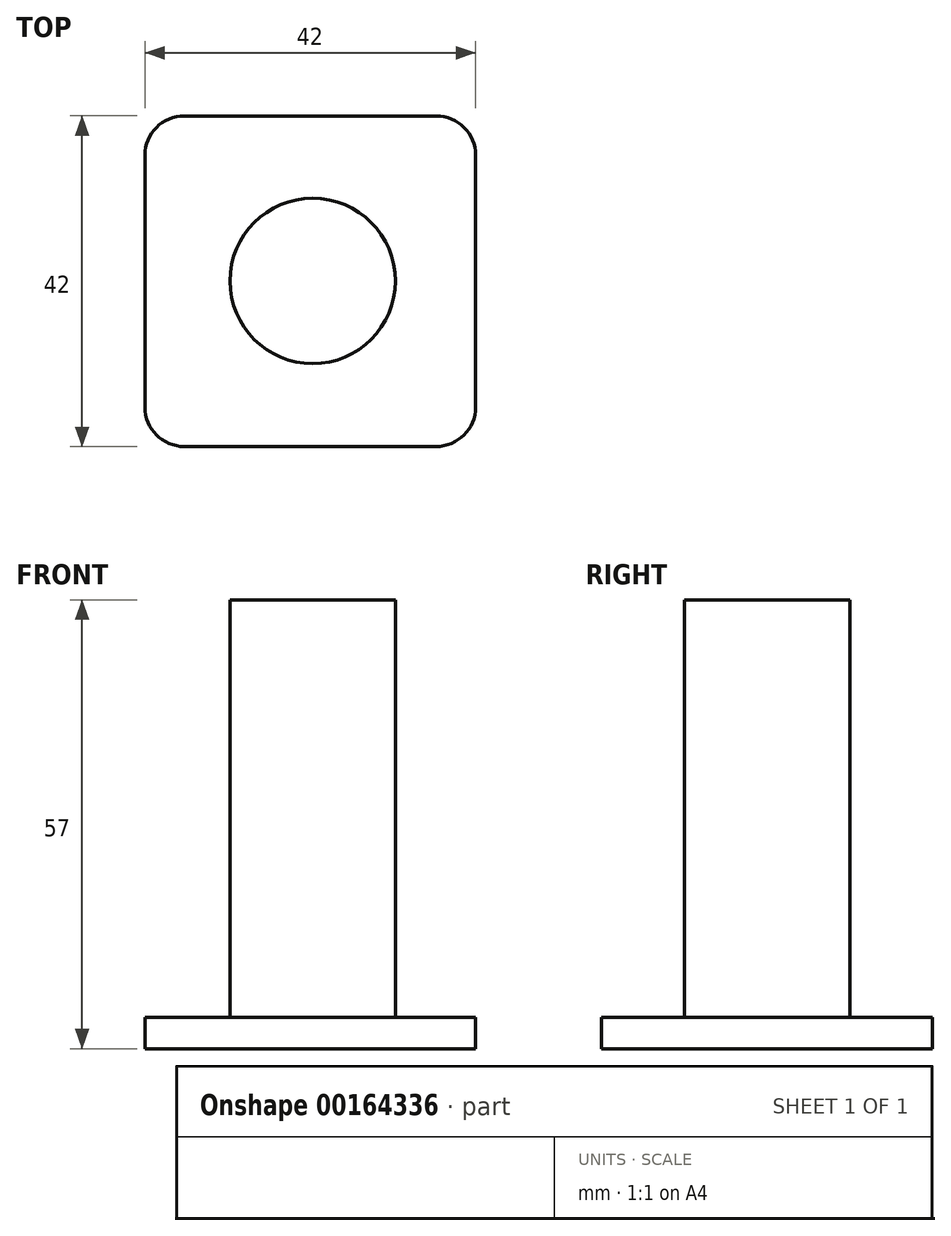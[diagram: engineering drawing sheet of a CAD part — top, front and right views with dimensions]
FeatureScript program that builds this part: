
annotation { "Feature Type Name" : "Feature", "Feature Type Description" : "" }
export const myFeature = defineFeature(function(context is Context, id is Id, definition is map)
    precondition{}
    {
        {
            var Q0;
            Q0=qCreatedBy(makeId("Top.planeOp"),FACE);
            var sketch = newSketch(context, id + "F0", { "sketchPlane" : qUnion([Q0])});
            skLineSegment(sketch, "E0.bottom", {"start": v(-21.31, 20.97) * mm, "end": v(20.69, 20.97) * mm});
            skLineSegment(sketch, "E0.top", {"start": v(-21.31, -21.03) * mm, "end": v(20.69, -21.03) * mm});
            skLineSegment(sketch, "E0.left", {"start": v(-21.31, 20.97) * mm, "end": v(-21.31, -21.03) * mm});
            skLineSegment(sketch, "E0.right", {"start": v(20.69, 20.97) * mm, "end": v(20.69, -21.03) * mm});
            skLineSegment(sketch, "E1", {"start": v(-21.31, -0.03) * mm, "end": v(20.69, -0.03) * mm, "construction": true});
            skCircle(sketch, "E2", {"center": v(0, 0) * mm, "radius": 10.5 * mm});
            skSolve(sketch);
        }
        {
            var Q0;
            Q0=makeQuery(id+"F0.imprint","IMPRINT",FACE,{"disambiguationData":[TD([[makeQuery(id+"F0.imprint","IMPRINT",EDGE,{"derivedFrom":sQuery(id+"F0.wireOp",EDGE,"E0.bottom")}),-1.0]])]});
            var Q1;
            Q1=makeQuery(id+"F0.imprint","IMPRINT",FACE,{"disambiguationData":[TD([[makeQuery(id+"F0.imprint","IMPRINT",EDGE,{"derivedFrom":sQuery(id+"F0.wireOp",EDGE,"E2")}),1.0]])]});
            extrude(context, id + "F1", {"entities" : qUnion([Q0, Q1]), "depth" : 4 * mm});
        }
        {
            var Q0;
            Q0=makeQuery(id+"F0.imprint","IMPRINT",FACE,{"disambiguationData":[TD([[makeQuery(id+"F0.imprint","IMPRINT",EDGE,{"derivedFrom":sQuery(id+"F0.wireOp",EDGE,"E2")}),1.0]])]});
            extrude(context, id + "F2", {"entities" : qUnion([Q0]), "operationType" : NewBodyOperationType.ADD, "depth" : 57 * mm});
        }
        {
            var Q0;
            Q0=makeQuery(id+"F1.opExtrude","SWEPT_EDGE",EDGE,{"disambiguationData":[OSD([sQuery(id+"F0.wireOp",EDGE,"E0.top"),sQuery(id+"F0.wireOp",EDGE,"E0.left")])]});
            var Q1;
            Q1=makeQuery(id+"F1.opExtrude","SWEPT_EDGE",EDGE,{"disambiguationData":[OSD([sQuery(id+"F0.wireOp",EDGE,"E0.bottom"),sQuery(id+"F0.wireOp",EDGE,"E0.left")])]});
            var Q2;
            Q2=makeQuery(id+"F1.opExtrude","SWEPT_EDGE",EDGE,{"disambiguationData":[OSD([sQuery(id+"F0.wireOp",EDGE,"E0.top"),sQuery(id+"F0.wireOp",EDGE,"E0.right")])]});
            var Q3;
            Q3=makeQuery(id+"F1.opExtrude","SWEPT_EDGE",EDGE,{"disambiguationData":[OSD([sQuery(id+"F0.wireOp",EDGE,"E0.bottom"),sQuery(id+"F0.wireOp",EDGE,"E0.right")])]});
            fillet(context, id + "F3", {"entities" : qUnion([Q0, Q1, Q2, Q3]), "radius" : 5 * mm, "tangentPropagation" : true, "allowEdgeOverflow" : false});
        }
    });
